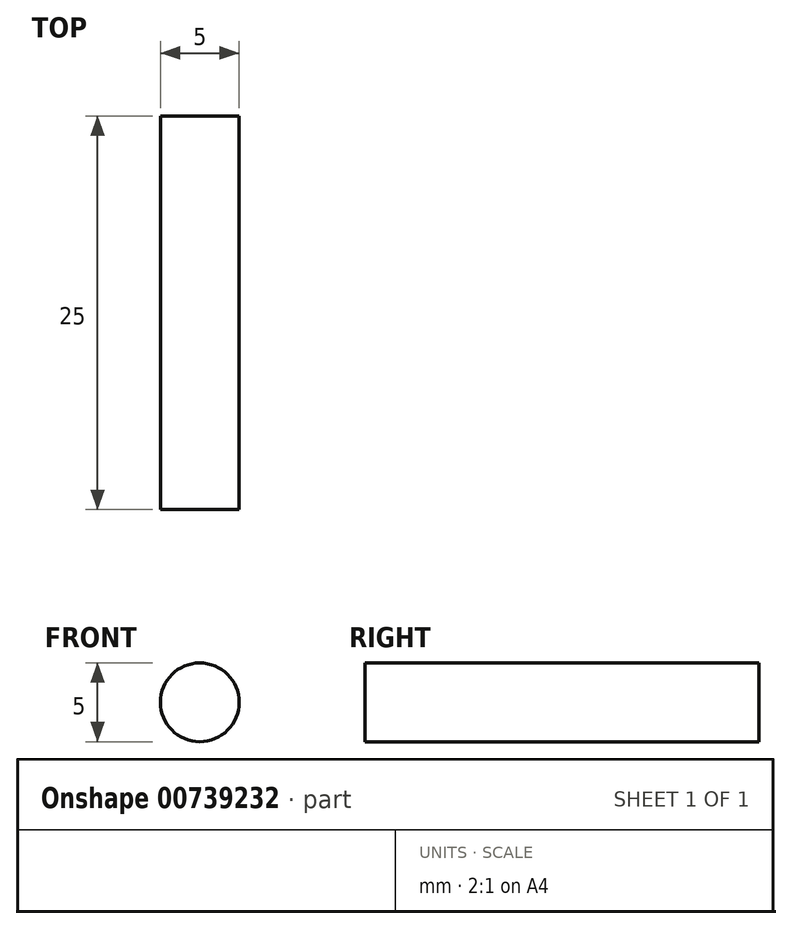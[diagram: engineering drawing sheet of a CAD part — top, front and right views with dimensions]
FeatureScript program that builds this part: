
annotation { "Feature Type Name" : "Feature", "Feature Type Description" : "" }
export const myFeature = defineFeature(function(context is Context, id is Id, definition is map)
    precondition{}
    {
        {
            var Q0;
            Q0=qCreatedBy(makeId("Front.planeOp"),FACE);
            var sketch = newSketch(context, id + "F0", { "sketchPlane" : qUnion([Q0])});
            skCircle(sketch, "E0", {"center": v(0, 0) * mm, "radius": 2.5 * mm});
            skSolve(sketch);
        }
        {
            var Q0;
            Q0 = qSketchRegion(id + "F0", true);
            extrude(context, id + "F1", {"entities" : qUnion([Q0]), "depth" : 25 * mm, "offsetDistance" : 25.4 * mm});
        }
    });
